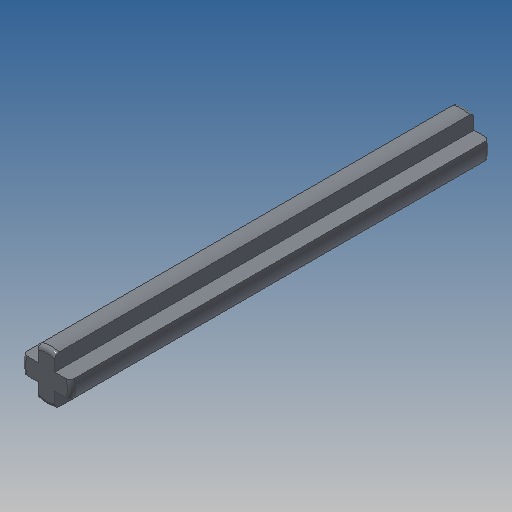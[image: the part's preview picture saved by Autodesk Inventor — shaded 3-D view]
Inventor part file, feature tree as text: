
AUTODESK INVENTOR PART (.ipt)
format: ipt  version: 2022.2 (Build 262287000, 287)  size: 140,288 bytes
history: native  units: in
note: dims shown in document units (in); Inventor stores cm internally (conversion verified against a paired STEP export)
features: extrude x1, fillet x1, sketch x1
ambient origin geometry x8: Origin, YZ Plane, XZ Plane, XY Plane, X Axis, Y Axis, Z Axis, Center Point
bodies: Solid1 (feature_tree)
feature tree (3):
  extrude  "Extrusion1"  Depth=0.0157in
  fillet  "Fillet1"  Radius=1.5748in
  sketch  "Sketch1"  dims[d0=0.189in d1=0.063in d2=1.5748in d3=0.0in d4=0.0157in d5=0.0in d6=0.0in]
